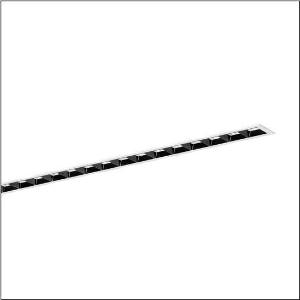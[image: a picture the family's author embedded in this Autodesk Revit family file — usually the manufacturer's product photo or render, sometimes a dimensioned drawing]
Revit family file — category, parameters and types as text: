
# Revit family: silica_21_51mx12db35wb
name_source: partatom
category: Lighting Fixtures
units: mm (PartAtom-declared; Revit-internal decimal feet)

## family parameters
Cut with Voids When Loaded = No
Host = Face
Light Source = No
Part Type = Normal
Room Calculation Point = No
Round Connector Dimension = Use Diameter
Shared = No

## types (1)
- --- (1 x LED, 5400 lm, 34.3 W, 3000K)
    Apparent Load = 34 VA
    CIE Flux Codes = 86 100 100 100 100
    Color Rendering = 80
    Color Temperature = 3000K
    Default Elevation = 1800 mm
    Description = Silica 21, office luminaire, primary light control with darklight reflector, of PMMA, black, CAT 2 (L<= 3000cd/m²), light emission: direct distribution, primary light characteristic: symmetric, installation type: recessed, LED, rated luminous flux: 5.400lm, luminous efficacy: 157lm/W, light colour: 830, colour temperature: 3000K, control gear: DALI 2, with terminal, 3+2-pole, max. 2.5mm², mains connection: 220..240V, AC, 50/60Hz, rated input power: 34.3W, luminaire housing, of aluminium, traffic white (RAL 9016), length: 1.528mm, width: 79mm, height: 53mm, protection rating (complete): IP20, insulation class (complete): insulation class I (protective earthing), certification: CE, ENEC, VDE, permissible operating ambient temperature: 0..+35°C, standard: EN 50419, packaging unit: 1 piece
    Height = 0 mm  [stored 0 ft]
    Lamp = 1 x LED
    Lamp Light Flux = 5400 lm
    Lamp Power = 34.3 W
    Lamp count = 1
    Length = 1527 mm
    Luminous efficacy = 157 lm/W
    Manufacturer = Siteco
    ModVariant = No
    Model = 51MX12DB35WB
    Mounting Place = Ceiling
    Mounting Type = Recessed
    Number of Poles = 1
    OnlyDefault = Yes
    Power Factor = 1
    Product Name = Silica 21
    Product group = office luminaire | ceiling recessed
    ProductGroupID = 400
    Protection Class = Protection class I
    Protection Degree = IP 20
    RLX_Detail_Level = 1
    RLX_Emergency_Light_Flux = 0 lm
    RLX_Emergency_Type = 0
    RLX_Emergency_Type_DB = No
    RlxData = <blob elided: 42221 chars, md5=e00a5dbf>
    Socket = socket
    Standby Power = 0 W
    System Light Flux = 5400 lm
    System Power = 34 W
    Type Comments = factory setting: luminous flux: 100 % | dim-lin: 254 | 392 mA
    Type Image = l_1335880.jpg
    URL = http://relux.com
    VarID = @adj_126143
    Voltage = 0 V
    Weight = 0.00 kg
    Width = 79 mm

note: [stored X ft] marks values corroborated as IEEE doubles in the binary element streams (Revit-internal decimal feet)

## geometry (parser evidence)
native form markers: Blend x4, Sweep x11
no freeform markers — native parametric forms only
